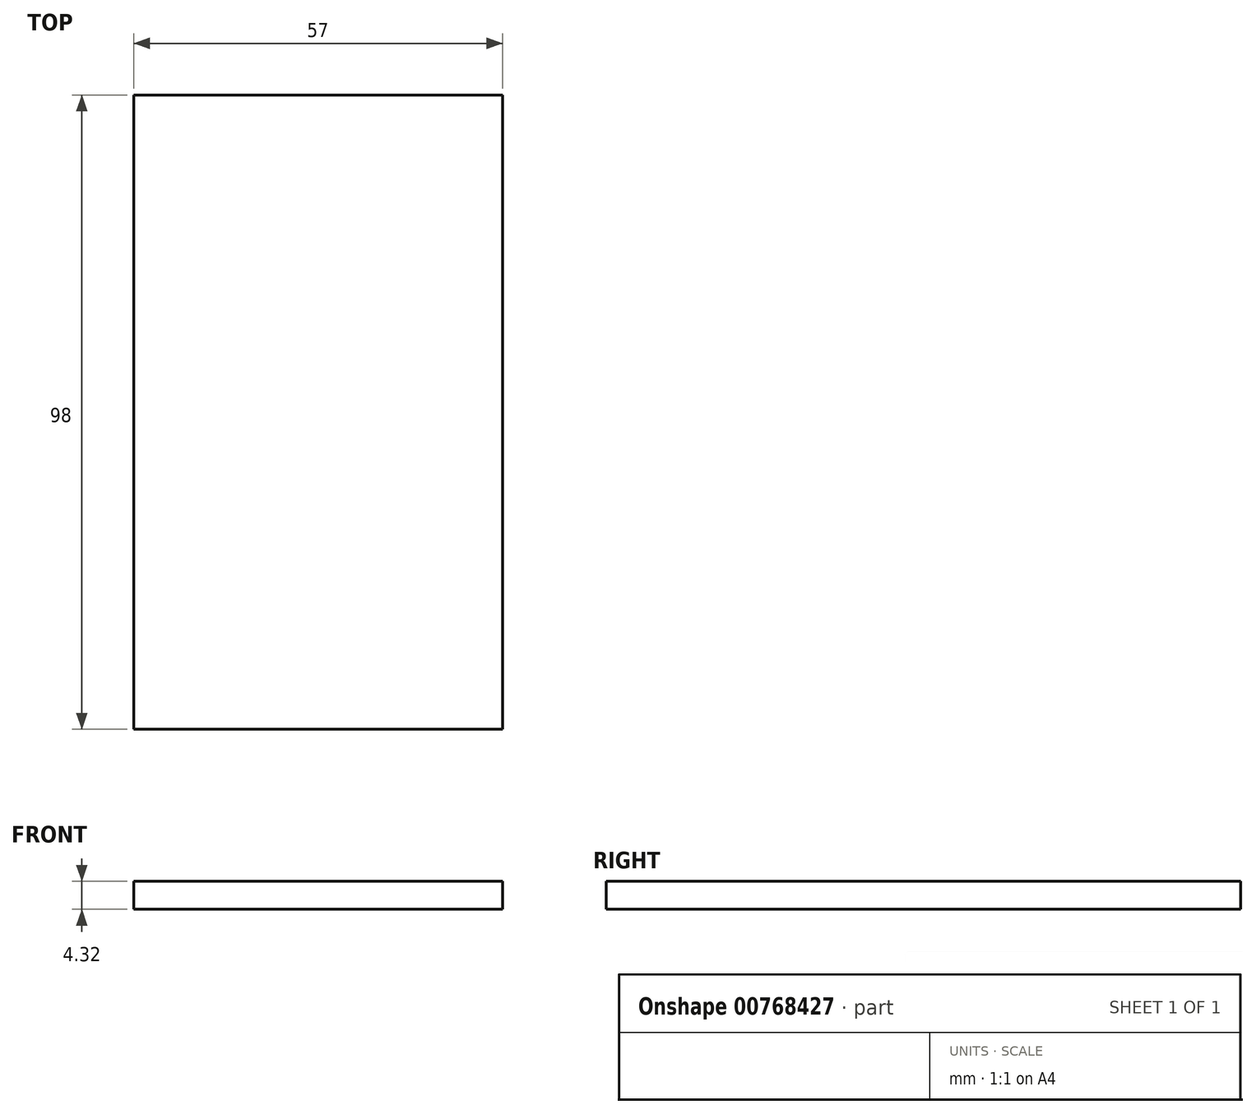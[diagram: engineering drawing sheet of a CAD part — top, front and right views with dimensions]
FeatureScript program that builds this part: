
annotation { "Feature Type Name" : "Feature", "Feature Type Description" : "" }
export const myFeature = defineFeature(function(context is Context, id is Id, definition is map)
    precondition{}
    {
        {
            var Q0;
            Q0=qCreatedBy(makeId("Top.planeOp"),FACE);
            var sketch = newSketch(context, id + "F0", { "sketchPlane" : qUnion([Q0])});
            skLineSegment(sketch, "E0.bottom", {"start": v(-29.51, 46.97) * mm, "end": v(27.49, 46.97) * mm});
            skLineSegment(sketch, "E0.top", {"start": v(-29.51, -51.03) * mm, "end": v(27.49, -51.03) * mm});
            skLineSegment(sketch, "E0.left", {"start": v(-29.51, 46.97) * mm, "end": v(-29.51, -51.03) * mm});
            skLineSegment(sketch, "E0.right", {"start": v(27.49, 46.97) * mm, "end": v(27.49, -51.03) * mm});
            skPoint(sketch, "E1", {"position": v(-571.2, 10112.35) * mm});
            skSolve(sketch);
        }
        {
            var Q0;
            Q0 = qSketchRegion(id + "F0", true);
            extrude(context, id + "F1", {"entities" : qUnion([Q0]), "depth" : 4.32 * mm, "offsetDistance" : 25.4 * mm});
        }
    });
